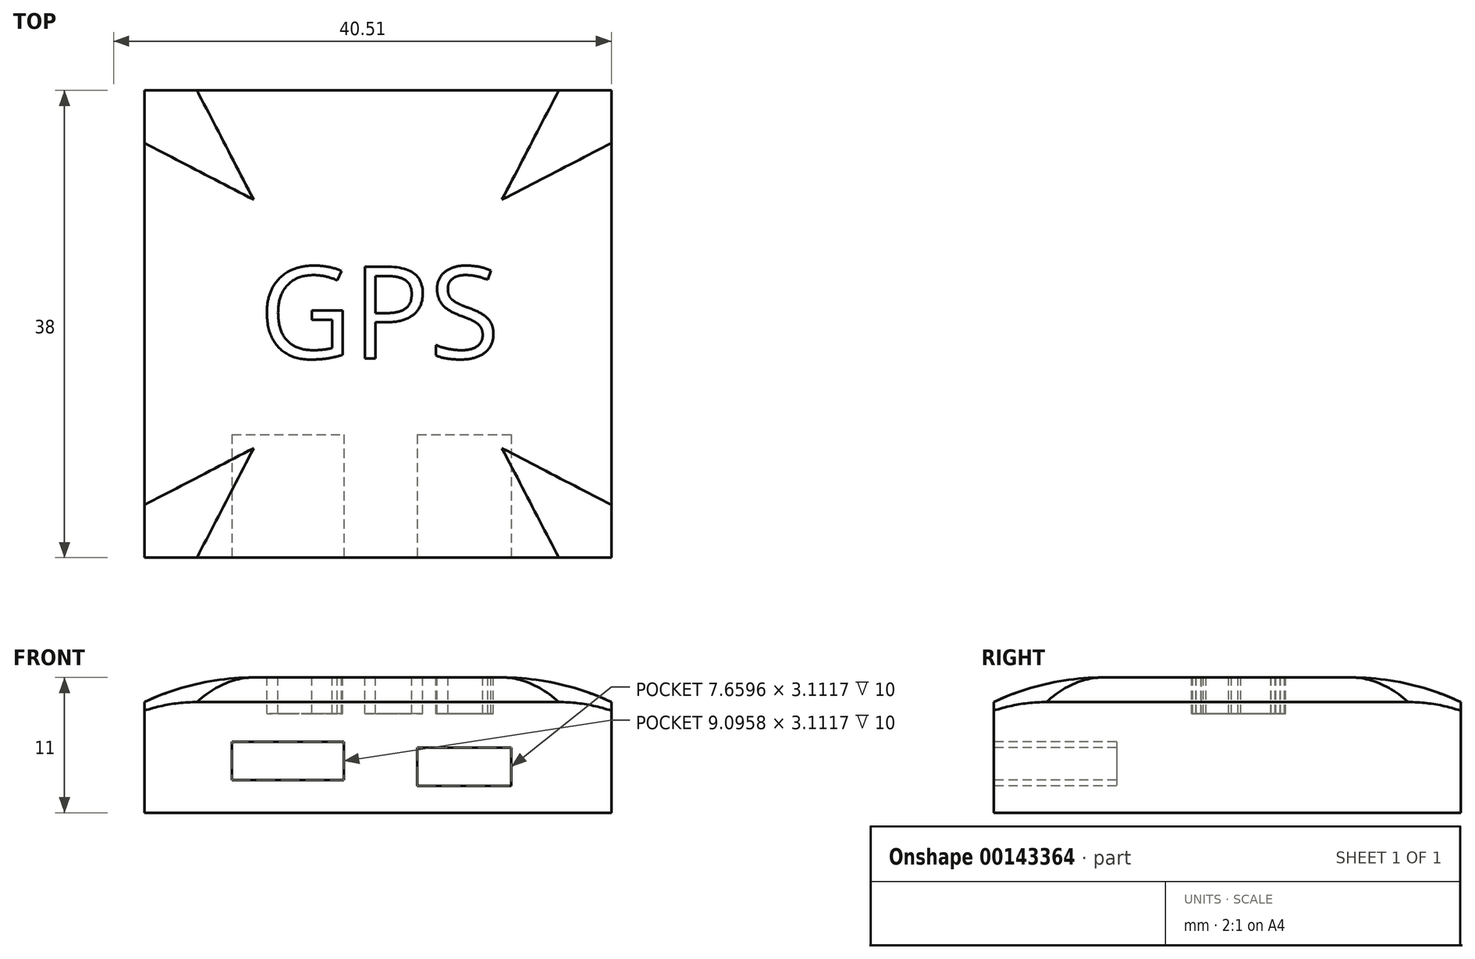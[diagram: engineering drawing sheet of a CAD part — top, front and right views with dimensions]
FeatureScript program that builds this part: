
annotation { "Feature Type Name" : "Feature", "Feature Type Description" : "" }
export const myFeature = defineFeature(function(context is Context, id is Id, definition is map)
    precondition{}
    {
        {
            var Q0;
            Q0=qCreatedBy(makeId("Top.planeOp"),FACE);
            var sketch = newSketch(context, id + "F0", { "sketchPlane" : qUnion([Q0])});
            skLineSegment(sketch, "E0.bottom", {"start": v(0, 0) * mm, "end": v(-38, 0) * mm});
            skLineSegment(sketch, "E0.top", {"start": v(0, 38) * mm, "end": v(-38, 38) * mm});
            skLineSegment(sketch, "E0.left", {"start": v(0, 0) * mm, "end": v(0, 38) * mm});
            skLineSegment(sketch, "E0.right", {"start": v(-38, 0) * mm, "end": v(-38, 38) * mm});
            skSolve(sketch);
        }
        {
            var Q0;
            Q0=makeQuery(id+"F0.imprint","IMPRINT",FACE,{"disambiguationData":[TD([[makeQuery(id+"F0.imprint","IMPRINT",EDGE,{"derivedFrom":sQuery(id+"F0.wireOp",EDGE,"E0.bottom")}),-1.0]])]});
            extrude(context, id + "F1", {"entities" : qUnion([Q0]), "depth" : 2 * mm});
        }
        {
            var Q0;
            Q0=makeQuery(id+"F1.opExtrude","CAP_EDGE",EDGE,{"disambiguationData":[OSD([sQuery(id+"F0.wireOp",EDGE,"E0.left")])],"isStart":false});
            var Q1;
            Q1=makeQuery(id+"F1.opExtrude","CAP_EDGE",EDGE,{"disambiguationData":[OSD([sQuery(id+"F0.wireOp",EDGE,"E0.bottom")])],"isStart":false});
            var Q2;
            Q2=makeQuery(id+"F1.opExtrude","CAP_EDGE",EDGE,{"disambiguationData":[OSD([sQuery(id+"F0.wireOp",EDGE,"E0.right")])],"isStart":false});
            var Q3;
            Q3=makeQuery(id+"F1.opExtrude","CAP_EDGE",EDGE,{"disambiguationData":[OSD([sQuery(id+"F0.wireOp",EDGE,"E0.top")])],"isStart":false});
            fillet(context, id + "F2", {"entities" : qUnion([Q0, Q1, Q2, Q3]), "radius" : 20.8 * mm, "tangentPropagation" : true, "allowEdgeOverflow" : false});
        }
        {
            var Q0;
            Q0=makeQuery(id+"F1.opExtrude","CAP_FACE",FACE,{"disambiguationData":[OSD([sQuery(id+"F0.wireOp",EDGE,"E0.bottom"),sQuery(id+"F0.wireOp",EDGE,"E0.top"),sQuery(id+"F0.wireOp",EDGE,"E0.left"),sQuery(id+"F0.wireOp",EDGE,"E0.right")])],"isStart":true});
            extrude(context, id + "F3", {"entities" : qUnion([Q0]), "operationType" : NewBodyOperationType.ADD, "depth" : 9 * mm});
        }
        {
            var Q0;
            {var subQ0=sQuery(id+"F0.wireOp",EDGE,"E0.right");var subQ1=sQuery(id+"F0.wireOp",EDGE,"E0.left");var subQ2=sQuery(id+"F0.wireOp",EDGE,"E0.top");var subQ3=sQuery(id+"F0.wireOp",EDGE,"E0.bottom");Q0=makeQuery(id+"F3.opExtrude","SWEPT_FACE",FACE,{"disambiguationData":[OSD([subQ3,subQ2,subQ1,subQ0]),TDD([makeQuery(id+"F2.opFillet","BLEND_EDGE",EDGE,{"blendedFrom":[makeQuery(id+"F1.opExtrude","CAP_EDGE",EDGE,{"disambiguationData":[OSD([subQ3])],"isStart":false}),makeQuery(id+"F1.opExtrude","CAP_FACE",FACE,{"disambiguationData":[OSD([subQ3,subQ2,subQ1,subQ0])],"isStart":true})],"blendedInto":[makeQuery(id+"F1.opExtrude","CAP_FACE",FACE,{"disambiguationData":[OSD([subQ3,subQ2,subQ1,subQ0])],"isStart":true})]})])]});}
            var sketch = newSketch(context, id + "F4", { "sketchPlane" : qUnion([Q0])});
            skLineSegment(sketch, "E1.bottom", {"start": v(-30.88, -3.23) * mm, "end": v(-21.78, -3.23) * mm});
            skLineSegment(sketch, "E1.top", {"start": v(-30.88, -6.34) * mm, "end": v(-21.78, -6.34) * mm});
            skLineSegment(sketch, "E1.left", {"start": v(-30.88, -3.23) * mm, "end": v(-30.88, -6.34) * mm});
            skLineSegment(sketch, "E1.right", {"start": v(-21.78, -3.23) * mm, "end": v(-21.78, -6.34) * mm});
            skLineSegment(sketch, "E2.bottom", {"start": v(-15.8, -3.71) * mm, "end": v(-8.14, -3.71) * mm});
            skLineSegment(sketch, "E2.top", {"start": v(-15.8, -6.82) * mm, "end": v(-8.14, -6.82) * mm});
            skLineSegment(sketch, "E2.left", {"start": v(-15.8, -3.71) * mm, "end": v(-15.8, -6.82) * mm});
            skLineSegment(sketch, "E2.right", {"start": v(-8.14, -3.71) * mm, "end": v(-8.14, -6.82) * mm});
            skSolve(sketch);
        }
        {
            var Q0;
            Q0=makeQuery(id+"F4.imprint","IMPRINT",FACE,{"disambiguationData":[TD([[makeQuery(id+"F4.imprint","IMPRINT",EDGE,{"derivedFrom":sQuery(id+"F4.wireOp",EDGE,"E1.bottom")}),-1.0]])]});
            var Q1;
            Q1=makeQuery(id+"F4.imprint","IMPRINT",FACE,{"disambiguationData":[TD([[makeQuery(id+"F4.imprint","IMPRINT",EDGE,{"derivedFrom":sQuery(id+"F4.wireOp",EDGE,"E2.bottom")}),-1.0]])]});
            extrude(context, id + "F5", {"entities" : qUnion([Q0, Q1]), "operationType" : NewBodyOperationType.REMOVE, "oppositeDirection" : true, "depth" : 10 * mm});
        }
        {
            var Q0;
            Q0=makeQuery(id+"F2.opFillet","BLEND_EDGE",EDGE,{"blendedFrom":[makeQuery(id+"F1.opExtrude","CAP_EDGE",EDGE,{"disambiguationData":[OSD([sQuery(id+"F0.wireOp",EDGE,"E0.bottom")])],"isStart":false}),makeQuery(id+"F1.opExtrude","CAP_EDGE",EDGE,{"disambiguationData":[OSD([sQuery(id+"F0.wireOp",EDGE,"E0.right")])],"isStart":false})],"blendedInto":[]});
            var Q1;
            Q1=makeQuery(id+"F2.opFillet","BLEND_EDGE",EDGE,{"blendedFrom":[makeQuery(id+"F1.opExtrude","CAP_EDGE",EDGE,{"disambiguationData":[OSD([sQuery(id+"F0.wireOp",EDGE,"E0.top")])],"isStart":false}),makeQuery(id+"F1.opExtrude","CAP_EDGE",EDGE,{"disambiguationData":[OSD([sQuery(id+"F0.wireOp",EDGE,"E0.right")])],"isStart":false})],"blendedInto":[]});
            var Q2;
            Q2=makeQuery(id+"F2.opFillet","BLEND_EDGE",EDGE,{"blendedFrom":[makeQuery(id+"F1.opExtrude","CAP_EDGE",EDGE,{"disambiguationData":[OSD([sQuery(id+"F0.wireOp",EDGE,"E0.top")])],"isStart":false}),makeQuery(id+"F1.opExtrude","CAP_EDGE",EDGE,{"disambiguationData":[OSD([sQuery(id+"F0.wireOp",EDGE,"E0.left")])],"isStart":false})],"blendedInto":[]});
            var Q3;
            Q3=makeQuery(id+"F2.opFillet","BLEND_EDGE",EDGE,{"blendedFrom":[makeQuery(id+"F1.opExtrude","CAP_EDGE",EDGE,{"disambiguationData":[OSD([sQuery(id+"F0.wireOp",EDGE,"E0.bottom")])],"isStart":false}),makeQuery(id+"F1.opExtrude","CAP_EDGE",EDGE,{"disambiguationData":[OSD([sQuery(id+"F0.wireOp",EDGE,"E0.left")])],"isStart":false})],"blendedInto":[]});
            fillet(context, id + "F6", {"entities" : qUnion([Q0, Q1, Q2, Q3]), "radius" : 10 * mm, "tangentPropagation" : true, "allowEdgeOverflow" : false});
        }
        {
            var Q0;
            Q0=makeQuery(id+"F1.opExtrude","CAP_FACE",FACE,{"disambiguationData":[OSD([sQuery(id+"F0.wireOp",EDGE,"E0.bottom"),sQuery(id+"F0.wireOp",EDGE,"E0.top"),sQuery(id+"F0.wireOp",EDGE,"E0.left"),sQuery(id+"F0.wireOp",EDGE,"E0.right")])],"isStart":false});
            var sketch = newSketch(context, id + "F7", { "sketchPlane" : qUnion([Q0])});
            skText(sketch, "E3", { "text": "GPS", "fontName": "OpenSans-Regular.ttf"});
            const initialGuessF7  = {"E3": [-0.02867, 0.01621, 1, 0, 0.0075]};
            skSetInitialGuess(sketch, initialGuessF7);
            skSolve(sketch);
        }
        {
            var Q0;
            Q0 = qSketchRegion(id + "F7", true);
            extrude(context, id + "F8", {"entities" : qUnion([Q0]), "operationType" : NewBodyOperationType.REMOVE, "oppositeDirection" : true, "depth" : 2.96 * mm});
        }
    });
